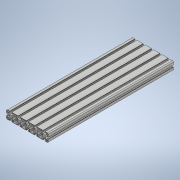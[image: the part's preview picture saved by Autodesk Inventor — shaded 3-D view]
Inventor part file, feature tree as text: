
AUTODESK INVENTOR PART (.ipt)
format: ipt  version: 2020 (Build 240168000, 168)  size: 573,440 bytes
history: native  units: mm
features: extrude x1, sketch x1
ambient origin geometry x8: Origin, YZ Plane, XZ Plane, XY Plane, X Axis, Y Axis, Z Axis, Center Point
bodies: Body1 (feature_tree)
feature tree (2):
  extrude  "Extrusion2"  Depth=300.0mm TaperAngle=0.0deg
  sketch  "Sketch1"  dims[d1=40.0mm d2=0.75mm d3=7.45mm d4=2.25mm d5=1.0mm d6=2.1mm d7=0.75mm d8=0.65mm d9=1.25mm d10=2.25mm d11=360.0deg d12=4.0mm d13=20.0mm d17=40.0mm d18=0.75mm d19=7.45mm d20=2.25mm d21=1.0mm d22=2.1mm d23=0.75mm d24=0.65mm d25=1.25mm d26=2.25mm d27=360.0deg d28=4.0mm d29=20.0mm d31=40.0mm d33=40.0mm d34=0.75mm d35=7.45mm d36=2.25mm d37=1.0mm d38=2.1mm d39=0.75mm d40=0.65mm d41=1.25mm d42=2.25mm d43=360.0deg d44=4.0mm d45=20.0mm d47=40.0mm d49=40.0mm d51=40.0mm d52=0.75mm d53=7.45mm d54=2.25mm d55=1.0mm d56=2.1mm d57=0.75mm d58=0.65mm d59=1.25mm d60=2.25mm d61=360.0deg d62=4.0mm d63=20.0mm d65=40.0mm d67=40.0mm d69=40.0mm d71=40.0mm d72=0.75mm d73=7.45mm d74=2.25mm d75=1.0mm d76=2.1mm d77=0.75mm d78=0.65mm d79=1.25mm d80=2.25mm d81=360.0deg d82=4.0mm d83=20.0mm d84=300.0mm d85=0.0mm]
